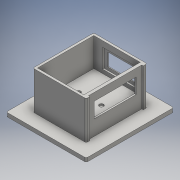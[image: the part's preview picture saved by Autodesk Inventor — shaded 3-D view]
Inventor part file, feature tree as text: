
AUTODESK INVENTOR PART (.ipt)
format: ipt  version: 2016 (Build 200138000, 138)  size: 244,224 bytes
history: native  units: mm
features: extrude x10, sketch x10
ambient origin geometry x8: Origin, YZ Plane, XZ Plane, XY Plane, X Axis, Y Axis, Z Axis, Center Point
bodies: Solid1 (feature_tree)
feature tree (20):
  extrude  "chamberBase"  Depth=85.0mm
  extrude  "chamberWallExt"  Depth=42.5mm
  extrude  "chamberIntExt"  Depth=10.0mm
  extrude  "rectCoverSlipMountExt"  Depth=10.0mm
  extrude  "rectCoverSlipWindow"  Depth=2.0mm
  extrude  "illObjExt"  Depth=70.0mm
  extrude  "viewingWindCoverSlipMount"  Depth=40.0mm
  extrude  "viewingWindExt"  Depth=2.0mm
  extrude  "sampleHolderMagnets"  Depth=3.0mm
  extrude  "xyStageMount"  Depth=37.5mm TaperAngle=0.0deg
  sketch  "Sketch1"  dims[d0=85.0mm d1=95.0mm]
  sketch  "Sketch2"  dims[d2=47.5mm d3=42.5mm]
  sketch  "Sketch3"  dims[d4=2.0mm d5=10.0mm]
  sketch  "Sketch4"  dims[d6=10.0mm d7=10.0mm]
  sketch  "Sketch5"  dims[d8=10.0mm d9=2.0mm]
  sketch  "Sketch7"  dims[d10=5.0mm d11=0.0mm d12=70.0mm]
  sketch  "Sketch8"  dims[d13=80.0mm d14=40.0mm]
  sketch  "Sketch9"  dims[d15=35.0mm d16=2.0mm]
  sketch  "Sketch10"  dims[d17=50.0mm d18=0.0mm d19=3.0mm]
  sketch  "Sketch13"  dims[d21=3.0mm d23=37.5mm d24=0.0mm d25=65.0mm d26=30.0mm d27=32.5mm d28=45.0mm d29=2.0mm d30=0.0mm d31=55.0mm d32=20.0mm d33=27.5mm d34=40.0mm d35=2.0mm d36=0.0mm d42=70.0mm d43=35.0mm d44=2.0mm d45=0.0mm d46=3.0mm d47=6.0mm d48=25.0mm d49=45.0mm d52=42.5mm d53=2.0mm d54=0.0mm d55=35.0mm d56=17.0mm d58=38.5mm d59=2.0mm d60=0.0mm d70=5.65mm d71=5.65mm d72=5.65mm d73=5.65mm d74=5.65mm d75=15.0mm d76=15.0mm d77=15.0mm d78=15.0mm d79=2.0mm d80=0.0mm d98=2.65mm d99=2.65mm d100=2.65mm d101=2.65mm d102=2.65mm d103=55.0mm d104=55.0mm d105=50.0mm d106=50.0mm d107=2.0mm d108=0.0mm d109=4.5mm d110=5.0mm]
